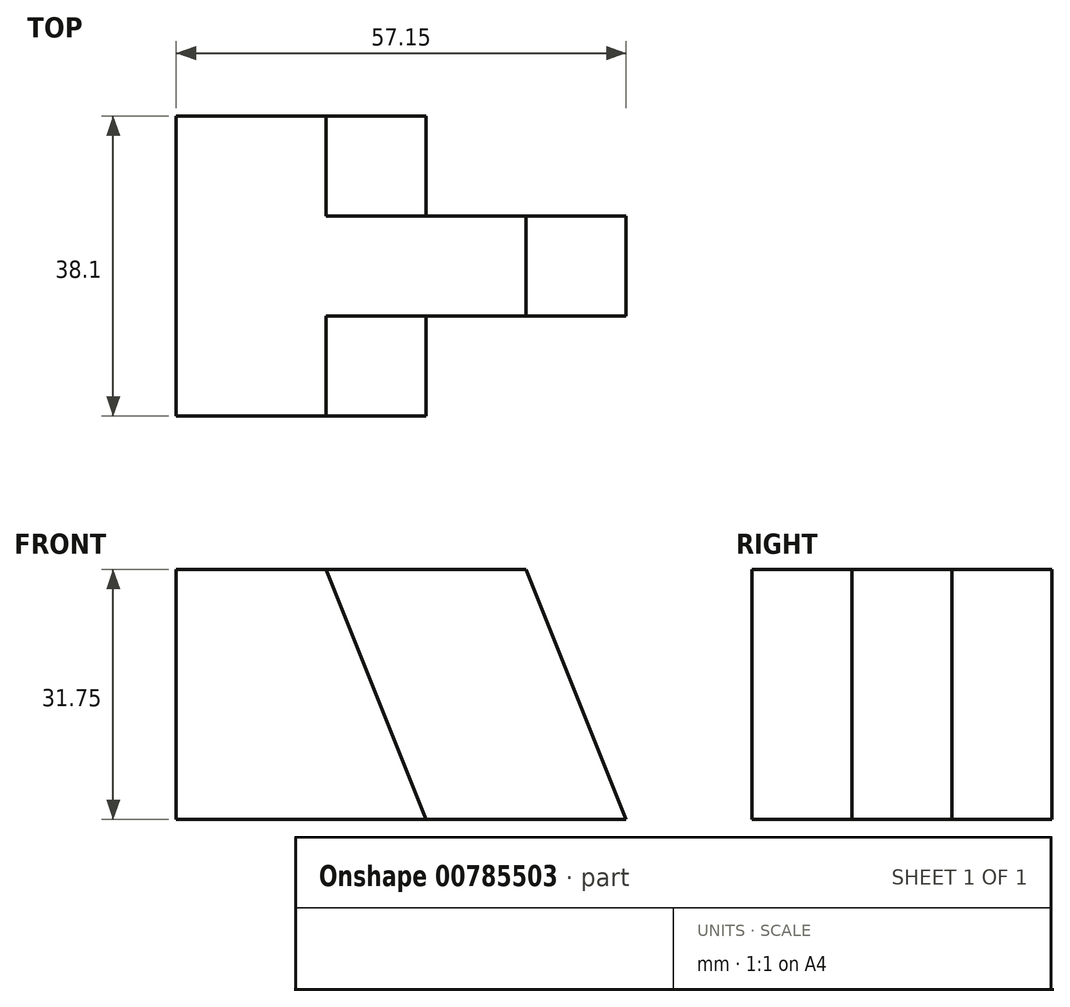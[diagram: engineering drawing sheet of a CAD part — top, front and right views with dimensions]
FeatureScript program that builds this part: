
annotation { "Feature Type Name" : "Feature", "Feature Type Description" : "" }
export const myFeature = defineFeature(function(context is Context, id is Id, definition is map)
    precondition{}
    {
        {
            var Q0;
            Q0=qCreatedBy(makeId("Front.planeOp"),FACE);
            var sketch = newSketch(context, id + "F0", { "sketchPlane" : qUnion([Q0])});
            skLineSegment(sketch, "E0", {"start": v(0, 0) * mm, "end": v(57.15, 0) * mm});
            skLineSegment(sketch, "E1", {"start": v(57.15, 0) * mm, "end": v(57.15, 31.75) * mm});
            skLineSegment(sketch, "E2", {"start": v(57.15, 31.75) * mm, "end": v(0, 31.75) * mm});
            skLineSegment(sketch, "E3", {"start": v(0, 31.75) * mm, "end": v(0, 0) * mm});
            skSolve(sketch);
        }
        {
            var Q0;
            Q0=makeQuery(id+"F0.imprint","IMPRINT",FACE,{"disambiguationData":[TD([[makeQuery(id+"F0.imprint","IMPRINT",EDGE,{"derivedFrom":sQuery(id+"F0.wireOp",EDGE,"E0")}),1.0]])]});
            extrude(context, id + "F1", {"entities" : qUnion([Q0]), "depth" : 38.1 * mm, "offsetDistance" : 25.4 * mm});
        }
        {
            var Q0;
            Q0=makeQuery(id+"F1.opExtrude","CAP_FACE",FACE,{"disambiguationData":[OSD([sQuery(id+"F0.wireOp",EDGE,"E0"),sQuery(id+"F0.wireOp",EDGE,"E1"),sQuery(id+"F0.wireOp",EDGE,"E2"),sQuery(id+"F0.wireOp",EDGE,"E3")])],"isStart":false});
            var sketch = newSketch(context, id + "F2", { "sketchPlane" : qUnion([Q0])});
            skLineSegment(sketch, "E4", {"start": v(19.05, 31.75) * mm, "end": v(57.15, 0) * mm});
            skLineSegment(sketch, "E5", {"start": v(19.05, 31.75) * mm, "end": v(57.15, 31.75) * mm});
            skLineSegment(sketch, "E6", {"start": v(57.15, 31.75) * mm, "end": v(57.15, 0) * mm});
            skSolve(sketch);
        }
        {
            var Q0;
            Q0=makeQuery(id+"F2.imprint","IMPRINT",FACE,{"disambiguationData":[TD([[makeQuery(id+"F2.imprint","IMPRINT",EDGE,{"derivedFrom":sQuery(id+"F2.wireOp",EDGE,"E4")}),1.0]])]});
            extrude(context, id + "F3", {"entities" : qUnion([Q0]), "operationType" : NewBodyOperationType.REMOVE, "oppositeDirection" : true, "depth" : 12.7 * mm, "offsetDistance" : 25.4 * mm});
        }
        {
            var Q0;
            Q0=makeQuery(id+"F1.opExtrude","CAP_FACE",FACE,{"disambiguationData":[OSD([sQuery(id+"F0.wireOp",EDGE,"E0"),sQuery(id+"F0.wireOp",EDGE,"E1"),sQuery(id+"F0.wireOp",EDGE,"E2"),sQuery(id+"F0.wireOp",EDGE,"E3")])],"isStart":true});
            var sketch = newSketch(context, id + "F4", { "sketchPlane" : qUnion([Q0])});
            skLineSegment(sketch, "E7", {"start": v(-57.15, 0) * mm, "end": v(-19.05, 31.75) * mm});
            skLineSegment(sketch, "E8", {"start": v(-57.15, 0) * mm, "end": v(-57.15, 31.75) * mm});
            skLineSegment(sketch, "E9", {"start": v(-57.15, 31.75) * mm, "end": v(-19.05, 31.75) * mm});
            skSolve(sketch);
        }
        {
            var Q0;
            Q0=makeQuery(id+"F4.imprint","IMPRINT",FACE,{"disambiguationData":[TD([[makeQuery(id+"F4.imprint","IMPRINT",EDGE,{"derivedFrom":sQuery(id+"F4.wireOp",EDGE,"E7")}),1.0]])]});
            extrude(context, id + "F5", {"entities" : qUnion([Q0]), "operationType" : NewBodyOperationType.REMOVE, "oppositeDirection" : true, "depth" : 12.7 * mm, "offsetDistance" : 25.4 * mm});
        }
        {
            var Q0;
            Q0=makeQuery(id+"F1.opExtrude","CAP_FACE",FACE,{"disambiguationData":[OSD([sQuery(id+"F0.wireOp",EDGE,"E0"),sQuery(id+"F0.wireOp",EDGE,"E1"),sQuery(id+"F0.wireOp",EDGE,"E2"),sQuery(id+"F0.wireOp",EDGE,"E3")])],"isStart":true});
            var sketch = newSketch(context, id + "F6", { "sketchPlane" : qUnion([Q0])});
            skLineSegment(sketch, "E10", {"start": v(-57.15, 0) * mm, "end": v(-31.75, 0) * mm});
            skLineSegment(sketch, "E11", {"start": v(-31.75, 0) * mm, "end": v(-19.05, 31.75) * mm});
            skLineSegment(sketch, "E12", {"start": v(-57.15, 0) * mm, "end": v(-19.05, 31.75) * mm});
            skLineSegment(sketch, "E13", {"start": v(-31.75, 0) * mm, "end": v(-57.15, 0) * mm});
            skSolve(sketch);
        }
        {
            var Q0;
            Q0=makeQuery(id+"F6.imprint","IMPRINT",FACE,{"disambiguationData":[TD([[makeQuery(id+"F6.imprint","IMPRINT",EDGE,{"derivedFrom":sQuery(id+"F6.wireOp",EDGE,"E11")}),1.0]])]});
            extrude(context, id + "F7", {"entities" : qUnion([Q0]), "operationType" : NewBodyOperationType.REMOVE, "oppositeDirection" : true, "depth" : 12.7 * mm, "offsetDistance" : 25.4 * mm});
        }
        {
            var Q0;
            Q0=makeQuery(id+"F7.boolean.opBoolean","MERGE",FACE,{"derivedFrom":[makeQuery(id+"F5.boolean.opBoolean","COPY",FACE,{"derivedFrom":makeQuery(id+"F5.opExtrude","CAP_FACE",FACE,{"disambiguationData":[OSD([sQuery(id+"F4.wireOp",EDGE,"E7"),sQuery(id+"F4.wireOp",EDGE,"E8"),sQuery(id+"F4.wireOp",EDGE,"E9")])],"isStart":false})}),makeQuery(id+"F7.opExtrude","CAP_FACE",FACE,{"disambiguationData":[OSD([sQuery(id+"F6.wireOp",EDGE,"E11"),sQuery(id+"F6.wireOp",EDGE,"E12"),sQuery(id+"F6.wireOp",EDGE,"E13")])],"isStart":false})]});
            var sketch = newSketch(context, id + "F8", { "sketchPlane" : qUnion([Q0])});
            skLineSegment(sketch, "E14", {"start": v(-44.45, 31.75) * mm, "end": v(-57.15, 0) * mm});
            skLineSegment(sketch, "E15", {"start": v(-57.15, 0) * mm, "end": v(-57.15, 31.75) * mm});
            skLineSegment(sketch, "E16", {"start": v(-57.15, 31.75) * mm, "end": v(-44.45, 31.75) * mm});
            skSolve(sketch);
        }
        {
            var Q0;
            Q0=makeQuery(id+"F8.imprint","IMPRINT",FACE,{"disambiguationData":[TD([[makeQuery(id+"F8.imprint","IMPRINT",EDGE,{"derivedFrom":sQuery(id+"F8.wireOp",EDGE,"E14")}),-1.0]])]});
            extrude(context, id + "F9", {"entities" : qUnion([Q0]), "operationType" : NewBodyOperationType.REMOVE, "oppositeDirection" : true, "depth" : 25.4 * mm, "offsetDistance" : 25.4 * mm});
        }
        {
            var Q0;
            Q0=makeQuery(id+"F1.opExtrude","CAP_FACE",FACE,{"disambiguationData":[OSD([sQuery(id+"F0.wireOp",EDGE,"E0"),sQuery(id+"F0.wireOp",EDGE,"E1"),sQuery(id+"F0.wireOp",EDGE,"E2"),sQuery(id+"F0.wireOp",EDGE,"E3")])],"isStart":false});
            var sketch = newSketch(context, id + "F10", { "sketchPlane" : qUnion([Q0])});
            skLineSegment(sketch, "E17", {"start": v(31.75, 0) * mm, "end": v(57.15, 0) * mm});
            skLineSegment(sketch, "E18", {"start": v(57.15, 0) * mm, "end": v(19.05, 31.75) * mm});
            skLineSegment(sketch, "E19", {"start": v(31.75, 0) * mm, "end": v(19.05, 31.75) * mm});
            skSolve(sketch);
        }
        {
            var Q0;
            Q0=makeQuery(id+"F10.imprint","IMPRINT",FACE,{"disambiguationData":[TD([[makeQuery(id+"F10.imprint","IMPRINT",EDGE,{"derivedFrom":sQuery(id+"F10.wireOp",EDGE,"E18")}),-1.0]])]});
            extrude(context, id + "F11", {"entities" : qUnion([Q0]), "operationType" : NewBodyOperationType.REMOVE, "oppositeDirection" : true, "depth" : 12.7 * mm, "offsetDistance" : 25.4 * mm});
        }
    });
